# Revit family: Sink-Undermount-ADA-Acorn-SUADA-1916_Series
name_source: partatom
category: Plumbing Fixtures
units: mm (PartAtom-declared; Revit-internal decimal feet)

## family parameters
Cut with Voids When Loaded = No
Host = Face
OmniClass Number = 23.45.05.14.14
OmniClass Title = Sinks/Lavatories
Part Type = Normal
Room Calculation Point = No
Round Connector Dimension = Use Diameter
Shared = Yes

## types (2) — shared parameters
ADA Compliant = Yes
Assembly Code = D2010440
CW Connection = No
CWFU = 3
Compliance Certifications = ASME A112.19.3/CSA B45.4, IAPMO® Certified for Conformance with Uniform Plumbing Code (UPC ), International Plumbing Code (IPC ), National Plumbing Code of Canada (NPC )
Countertop Thickness = 1/2"
Default Elevation = 34"
Description = Acorn-Sinks® Stainless Steel ADA Undermount Sink, 19" x 16"
Drain Size = 3 1/2"
Finish = Stainless Steel-18 Gauge-Type 304-Acorn-Satin
HW Connection = No
HWFU = 3
Installation Type = Undermount
Length = 18 1/2"
Manufacturer = Acorn
Product Documentation Link = https://www.acorneng.com
Product Page URL = https://www.acorneng.com
Sink Bowl Length = 16"
Sink Bowl Width = 19"
URL = https://www.acorneng.com
Vent Connection = No
WFU = 4
Waste Connection = No
Width = 21 1/2"
cUPC Compliant = Yes

## per-type parameters (varying)
| type | -45 4-1/2” Deep Bowl | -55 5-1/2” Deep Bowl | Sink Bowl Depth |
| SUADA-1916-45 | Yes | No | 4 1/2" |
| SUADA-1916-55 | No | Yes | 5 1/2" |

note: column(s) folded — value = type name in every type: Model

## geometry (parser evidence)
native form markers: Sweep x3
no freeform markers — native parametric forms only
